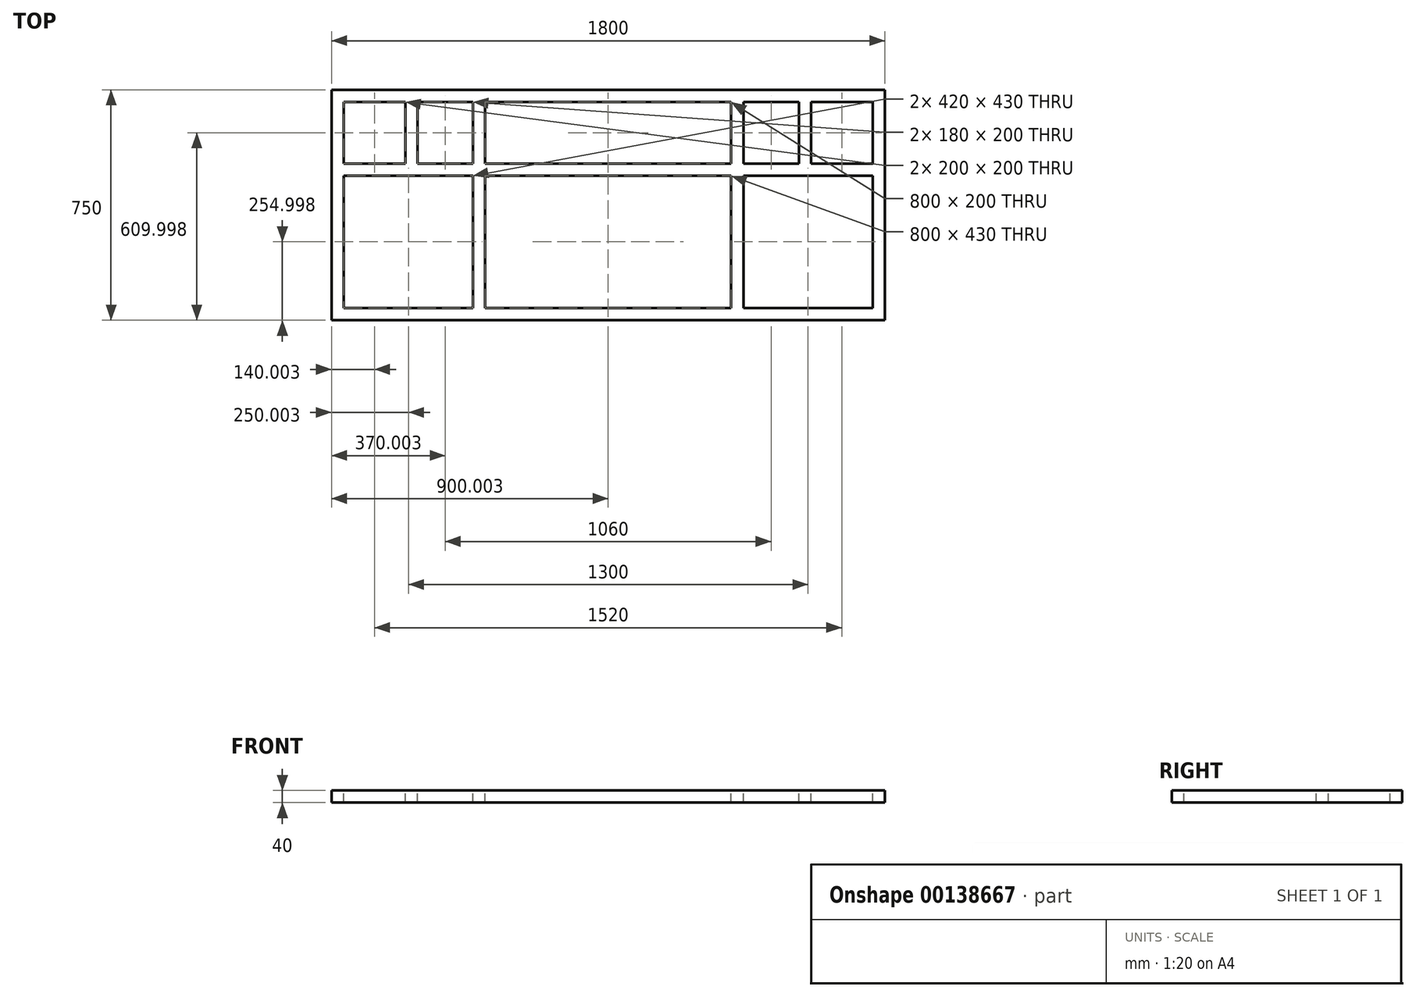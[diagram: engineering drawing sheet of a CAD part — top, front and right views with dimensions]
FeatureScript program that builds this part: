
annotation { "Feature Type Name" : "Feature", "Feature Type Description" : "" }
export const myFeature = defineFeature(function(context is Context, id is Id, definition is map)
    precondition{}
    {
        {
            var Q0;
            Q0=qCreatedBy(makeId("Top.planeOp"),FACE);
            var sketch = newSketch(context, id + "F0", { "sketchPlane" : qUnion([Q0])});
            skLineSegment(sketch, "E0.bottom", {"start": v(-891.08, 123.68) * mm, "end": v(908.92, 123.68) * mm});
            skLineSegment(sketch, "E0.top", {"start": v(-891.08, -626.32) * mm, "end": v(908.92, -626.32) * mm});
            skLineSegment(sketch, "E0.left", {"start": v(-891.08, 123.68) * mm, "end": v(-891.08, -626.32) * mm});
            skLineSegment(sketch, "E0.right", {"start": v(908.92, 123.68) * mm, "end": v(908.92, -626.32) * mm});
            skSolve(sketch);
        }
        {
            var Q0;
            Q0 = qSketchRegion(id + "F0", true);
            extrude(context, id + "F1", {"entities" : qUnion([Q0]), "depth" : 40 * mm});
        }
        {
            var Q0;
            Q0=makeQuery(id+"F1.opExtrude","CAP_FACE",FACE,{"disambiguationData":[OSD([sQuery(id+"F0.wireOp",EDGE,"E0.bottom"),sQuery(id+"F0.wireOp",EDGE,"E0.top"),sQuery(id+"F0.wireOp",EDGE,"E0.left"),sQuery(id+"F0.wireOp",EDGE,"E0.right")])],"isStart":false});
            var sketch = newSketch(context, id + "F2", { "sketchPlane" : qUnion([Q0])});
            skLineSegment(sketch, "E1.bottom", {"start": v(-851.08, -156.32) * mm, "end": v(-431.08, -156.32) * mm});
            skLineSegment(sketch, "E1.top", {"start": v(-851.08, -586.32) * mm, "end": v(-431.08, -586.32) * mm});
            skLineSegment(sketch, "E1.left", {"start": v(-851.08, -156.32) * mm, "end": v(-851.08, -586.32) * mm});
            skLineSegment(sketch, "E1.right", {"start": v(-431.08, -156.32) * mm, "end": v(-431.08, -586.32) * mm});
            skLineSegment(sketch, "E2.bottom", {"start": v(-391.08, -156.32) * mm, "end": v(408.92, -156.32) * mm});
            skLineSegment(sketch, "E2.top", {"start": v(-391.08, -586.32) * mm, "end": v(408.92, -586.32) * mm});
            skLineSegment(sketch, "E2.left", {"start": v(-391.08, -156.32) * mm, "end": v(-391.08, -586.32) * mm});
            skLineSegment(sketch, "E2.right", {"start": v(408.92, -156.32) * mm, "end": v(408.92, -586.32) * mm});
            skLineSegment(sketch, "E3.bottom", {"start": v(-851.08, 83.68) * mm, "end": v(-651.08, 83.68) * mm});
            skLineSegment(sketch, "E3.top", {"start": v(-851.08, -116.32) * mm, "end": v(-651.08, -116.32) * mm});
            skLineSegment(sketch, "E3.left", {"start": v(-851.08, 83.68) * mm, "end": v(-851.08, -116.32) * mm});
            skLineSegment(sketch, "E3.right", {"start": v(-651.08, 83.68) * mm, "end": v(-651.08, -116.32) * mm});
            skLineSegment(sketch, "E4.bottom", {"start": v(668.92, 83.68) * mm, "end": v(868.92, 83.68) * mm});
            skLineSegment(sketch, "E4.top", {"start": v(668.92, -116.32) * mm, "end": v(868.92, -116.32) * mm});
            skLineSegment(sketch, "E4.left", {"start": v(668.92, 83.68) * mm, "end": v(668.92, -116.32) * mm});
            skLineSegment(sketch, "E4.right", {"start": v(868.92, 83.68) * mm, "end": v(868.92, -116.32) * mm});
            skLineSegment(sketch, "E5.bottom", {"start": v(448.92, -156.32) * mm, "end": v(868.92, -156.32) * mm});
            skLineSegment(sketch, "E5.top", {"start": v(448.92, -586.32) * mm, "end": v(868.92, -586.32) * mm});
            skLineSegment(sketch, "E5.left", {"start": v(448.92, -156.32) * mm, "end": v(448.92, -586.32) * mm});
            skLineSegment(sketch, "E5.right", {"start": v(868.92, -156.32) * mm, "end": v(868.92, -586.32) * mm});
            skLineSegment(sketch, "E6.bottom", {"start": v(-431.08, -116.32) * mm, "end": v(-611.08, -116.32) * mm});
            skLineSegment(sketch, "E6.top", {"start": v(-431.08, 83.68) * mm, "end": v(-611.08, 83.68) * mm});
            skLineSegment(sketch, "E6.left", {"start": v(-431.08, -116.32) * mm, "end": v(-431.08, 83.68) * mm});
            skLineSegment(sketch, "E6.right", {"start": v(-611.08, -116.32) * mm, "end": v(-611.08, 83.68) * mm});
            skLineSegment(sketch, "E7.bottom", {"start": v(448.92, -116.32) * mm, "end": v(628.92, -116.32) * mm});
            skLineSegment(sketch, "E7.top", {"start": v(448.92, 83.68) * mm, "end": v(628.92, 83.68) * mm});
            skLineSegment(sketch, "E7.left", {"start": v(448.92, -116.32) * mm, "end": v(448.92, 83.68) * mm});
            skLineSegment(sketch, "E7.right", {"start": v(628.92, -116.32) * mm, "end": v(628.92, 83.68) * mm});
            skLineSegment(sketch, "E8.bottom", {"start": v(-391.08, 83.68) * mm, "end": v(408.92, 83.68) * mm});
            skLineSegment(sketch, "E8.top", {"start": v(-391.08, -116.32) * mm, "end": v(408.92, -116.32) * mm});
            skLineSegment(sketch, "E8.left", {"start": v(-391.08, 83.68) * mm, "end": v(-391.08, -116.32) * mm});
            skLineSegment(sketch, "E8.right", {"start": v(408.92, 83.68) * mm, "end": v(408.92, -116.32) * mm});
            skSolve(sketch);
        }
        {
            var Q0;
            Q0 = qSketchRegion(id + "F2", true);
            extrude(context, id + "F3", {"entities" : qUnion([Q0]), "operationType" : NewBodyOperationType.REMOVE, "oppositeDirection" : true, "depth" : 40 * mm});
        }
    });
